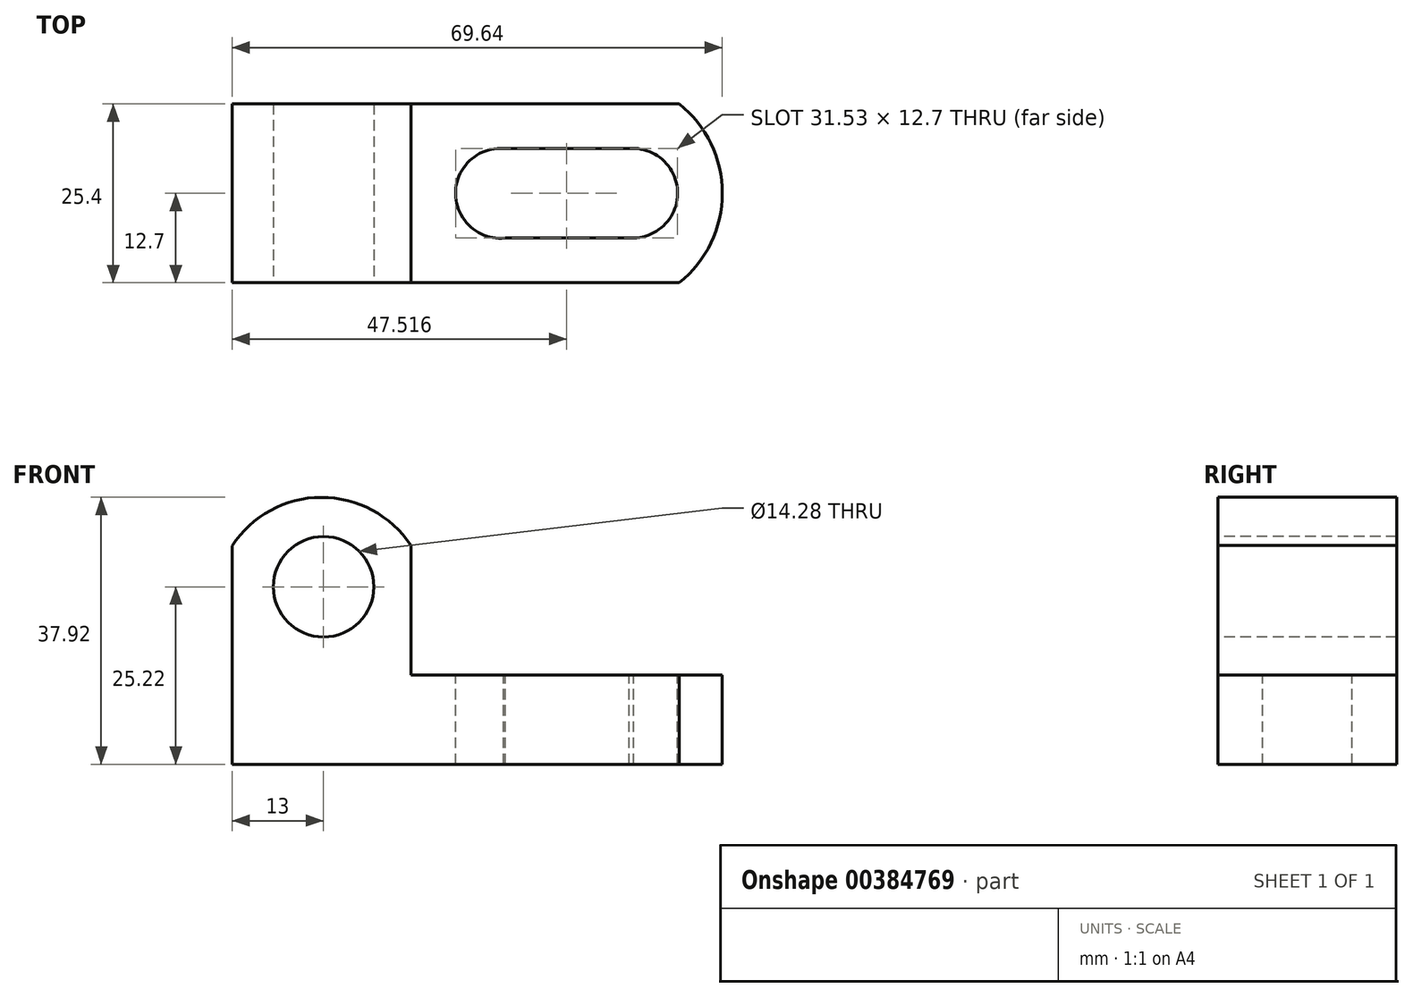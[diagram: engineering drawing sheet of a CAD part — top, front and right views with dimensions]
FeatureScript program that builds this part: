
annotation { "Feature Type Name" : "Feature", "Feature Type Description" : "" }
export const myFeature = defineFeature(function(context is Context, id is Id, definition is map)
    precondition{}
    {
        {
            var Q0;
            Q0=qCreatedBy(makeId("Front.planeOp"),FACE);
            var sketch = newSketch(context, id + "F0", { "sketchPlane" : qUnion([Q0])});
            skLineSegment(sketch, "E0", {"start": v(0, 38.1) * mm, "end": v(0, 0) * mm});
            skLineSegment(sketch, "E1", {"start": v(0, 0) * mm, "end": v(69.85, 0) * mm});
            skLineSegment(sketch, "E2", {"start": v(69.85, 0) * mm, "end": v(69.85, 12.7) * mm});
            skLineSegment(sketch, "E3", {"start": v(69.85, 12.7) * mm, "end": v(25.4, 12.7) * mm});
            skLineSegment(sketch, "E4", {"start": v(25.4, 12.7) * mm, "end": v(25.4, 38.1) * mm});
            skLineSegment(sketch, "E5", {"start": v(0, 38.1) * mm, "end": v(25.4, 38.1) * mm});
            skSolve(sketch);
        }
        {
            var Q0;
            Q0=makeQuery(id+"F0.imprint","IMPRINT",FACE,{"disambiguationData":[TD([[makeQuery(id+"F0.imprint","IMPRINT",EDGE,{"derivedFrom":sQuery(id+"F0.wireOp",EDGE,"E0")}),1.0]])]});
            extrude(context, id + "F1", {"entities" : qUnion([Q0]), "depth" : 25.4 * mm});
        }
        {
            var Q0;
            Q0=makeQuery(id+"F1.opExtrude","CAP_FACE",FACE,{"disambiguationData":[OSD([sQuery(id+"F0.wireOp",EDGE,"E0"),sQuery(id+"F0.wireOp",EDGE,"E1"),sQuery(id+"F0.wireOp",EDGE,"E2"),sQuery(id+"F0.wireOp",EDGE,"E3"),sQuery(id+"F0.wireOp",EDGE,"E4"),sQuery(id+"F0.wireOp",EDGE,"E5")])],"isStart":false});
            var sketch = newSketch(context, id + "F2", { "sketchPlane" : qUnion([Q0])});
            skArc(sketch, "E6", {"start": v(25.4, 31.06) * mm, "mid": v(12.68, 37.92) * mm, "end": v(0, 31) * mm});
            skLineSegment(sketch, "E7", {"start": v(0, 31) * mm, "end": v(0, 38.1) * mm});
            skLineSegment(sketch, "E8", {"start": v(0, 38.1) * mm, "end": v(25.4, 38.1) * mm});
            skLineSegment(sketch, "E9", {"start": v(25.4, 38.1) * mm, "end": v(25.4, 31.06) * mm});
            skSolve(sketch);
        }
        {
            var Q0;
            Q0=makeQuery(id+"F2.imprint","IMPRINT",FACE,{"disambiguationData":[TD([[makeQuery(id+"F2.imprint","IMPRINT",EDGE,{"derivedFrom":sQuery(id+"F2.wireOp",EDGE,"E6")}),-1.0]])]});
            extrude(context, id + "F3", {"entities" : qUnion([Q0]), "operationType" : NewBodyOperationType.REMOVE, "oppositeDirection" : true, "depth" : 25.4 * mm});
        }
        {
            var Q0;
            Q0=makeQuery(id+"F1.opExtrude","SWEPT_FACE",FACE,{"disambiguationData":[OSD([sQuery(id+"F0.wireOp",EDGE,"E3")])]});
            var sketch = newSketch(context, id + "F4", { "sketchPlane" : qUnion([Q0])});
            skArc(sketch, "E10", {"start": v(63.53, -25.4) * mm, "mid": v(69.64, -12.7) * mm, "end": v(63.53, 0) * mm});
            skSolve(sketch);
        }
        {
            var Q0;
            {var subQ0=sQuery(id+"F4.wireOp",EDGE,"E10");Q0=makeQuery(id+"F4.imprint","IMPRINT",FACE,{"disambiguationData":[TD([[makeQuery(id+"F4.imprint","IMPRINT",EDGE,{"derivedFrom":subQ0}),-1.0]])]});}
            extrude(context, id + "F5", {"entities" : qUnion([Q0]), "operationType" : NewBodyOperationType.REMOVE, "oppositeDirection" : true, "depth" : 25.4 * mm});
        }
        {
            var Q0;
            Q0=makeQuery(id+"F1.opExtrude","CAP_FACE",FACE,{"disambiguationData":[OSD([sQuery(id+"F0.wireOp",EDGE,"E0"),sQuery(id+"F0.wireOp",EDGE,"E1"),sQuery(id+"F0.wireOp",EDGE,"E2"),sQuery(id+"F0.wireOp",EDGE,"E3"),sQuery(id+"F0.wireOp",EDGE,"E4"),sQuery(id+"F0.wireOp",EDGE,"E5")])],"isStart":false});
            var sketch = newSketch(context, id + "F6", { "sketchPlane" : qUnion([Q0])});
            skCircle(sketch, "E11", {"center": v(13, 25.22) * mm, "radius": 7.14 * mm});
            skSolve(sketch);
        }
        {
            var Q0;
            Q0=makeQuery(id+"F6.imprint","IMPRINT",FACE,{"disambiguationData":[TD([[makeQuery(id+"F6.imprint","IMPRINT",EDGE,{"derivedFrom":sQuery(id+"F6.wireOp",EDGE,"E11")}),1.0]])]});
            extrude(context, id + "F7", {"entities" : qUnion([Q0]), "operationType" : NewBodyOperationType.REMOVE, "oppositeDirection" : true, "depth" : 25.4 * mm});
        }
        {
            var Q0;
            Q0=makeQuery(id+"F1.opExtrude","SWEPT_FACE",FACE,{"disambiguationData":[OSD([sQuery(id+"F0.wireOp",EDGE,"E3")])]});
            var sketch = newSketch(context, id + "F8", { "sketchPlane" : qUnion([Q0])});
            skArc(sketch, "E12", {"start": v(38.56, -6.35) * mm, "mid": v(31.75, -12.82) * mm, "end": v(38.79, -19.05) * mm});
            skArc(sketch, "E13", {"start": v(57.06, -19.05) * mm, "mid": v(63.28, -12.35) * mm, "end": v(56.39, -6.35) * mm});
            skLineSegment(sketch, "E14", {"start": v(38.56, -6.35) * mm, "end": v(56.39, -6.35) * mm});
            skLineSegment(sketch, "E15", {"start": v(57.06, -19.05) * mm, "end": v(38.79, -19.05) * mm});
            skSolve(sketch);
        }
        {
            var Q0;
            Q0=makeQuery(id+"F8.imprint","IMPRINT",FACE,{"disambiguationData":[TD([[makeQuery(id+"F8.imprint","IMPRINT",EDGE,{"derivedFrom":sQuery(id+"F8.wireOp",EDGE,"E12")}),1.0]])]});
            extrude(context, id + "F9", {"entities" : qUnion([Q0]), "operationType" : NewBodyOperationType.REMOVE, "oppositeDirection" : true, "depth" : 25.4 * mm});
        }
    });
